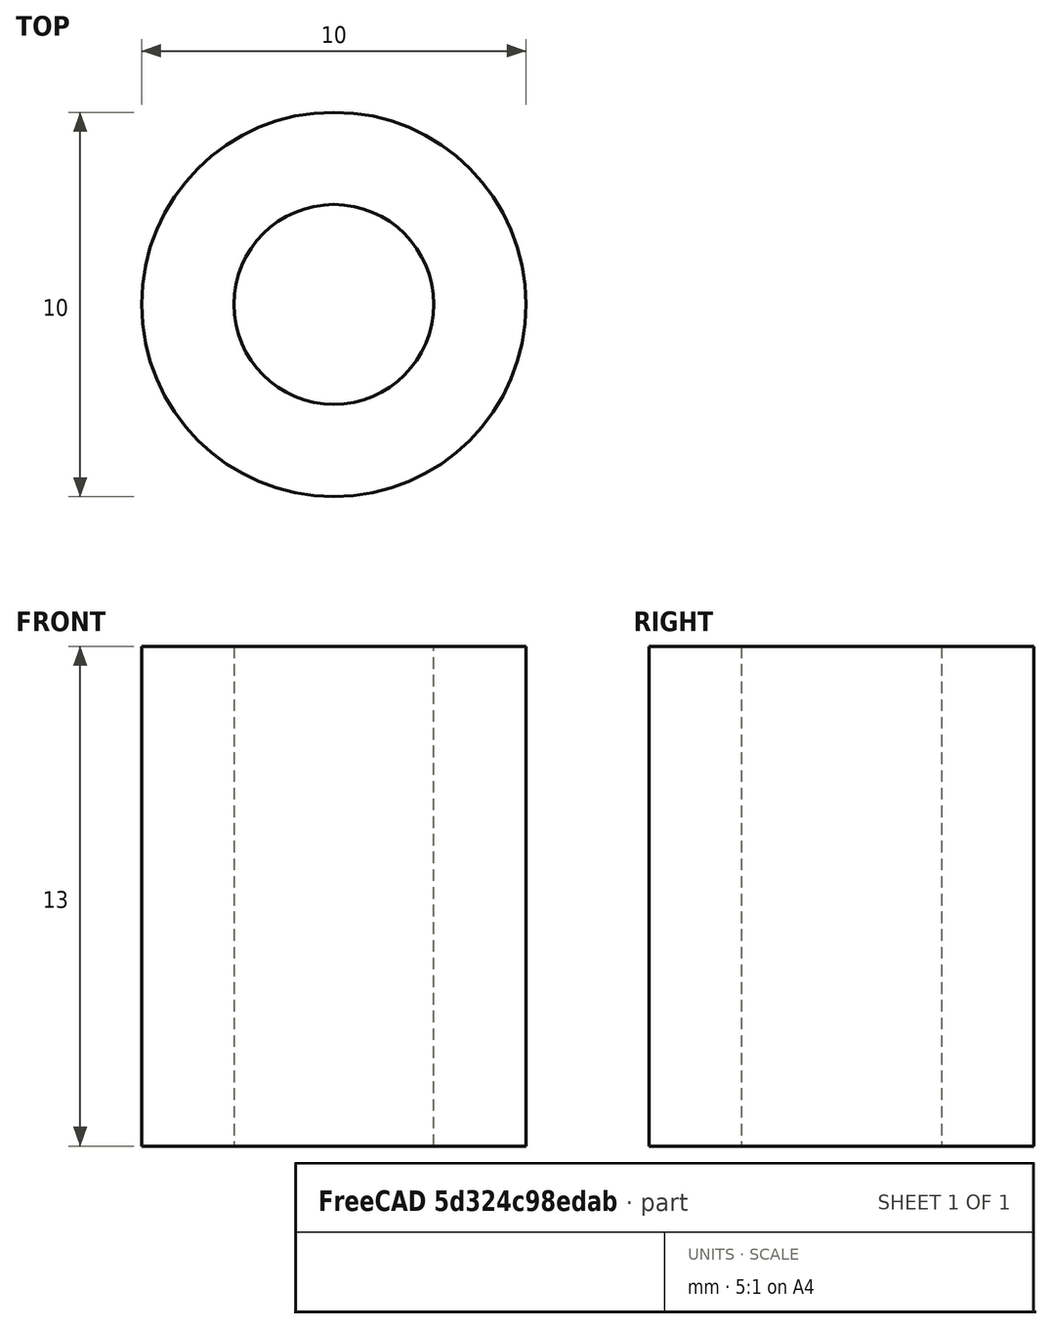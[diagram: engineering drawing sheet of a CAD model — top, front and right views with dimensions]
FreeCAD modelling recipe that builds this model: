
FCSTD DOCUMENT  (FreeCAD 1.0R38806 (Git))
Label: idler_spacer_13
License: All rights reserved
LicenseURL: http://en.wikipedia.org/wiki/All_rights_reserved
objects: Sketcher::SketchObject×1, PartDesign::Pad×1, PartDesign::Body×1
note: 6 computed .brp shape members not serialized (recipe doc carries the construction recipe); baked Part::Feature solids carry a one-line shape summary decoded from their .brp

FEATURE [Sketcher::SketchObject] Sketch
  ArcFitTolerance = 1e-06
  AttachmentSupport = -> [XY_Plane]
  FullyConstrained = true
  MakeInternals = false
  MapMode = 5
  sketch-geometry (2):
    g0: Circle CenterX=0 CenterY=0 CenterZ=0 NormalX=0 NormalY=0 NormalZ=1 AngleXU=0 Radius=5
    g1: Circle CenterX=0 CenterY=0 CenterZ=0 NormalX=0 NormalY=0 NormalZ=1 AngleXU=0 Radius=2.6
  constraints (5):
    c: Coincident(g0,g-1)
    c: PointOnObject(g1,g-1)
    c: Diameter(g0) = 10
    c: Diameter(g1) = 5.2
    c: DistanceX(g0,g1) = 0
FEATURE [PartDesign::Pad] Pad
  Direction = (0,0,1)
  Length = 13
  Length2 = 10
  Profile = -> Sketch
  ReferenceAxis = -> Sketch [N_Axis]
  Suppressed = false
  Type = 0
FEATURE [PartDesign::Body] Body
  AllowCompound = false
  Group = -> [Sketch,Pad]
  Origin = -> Origin
  Tip = -> Pad
